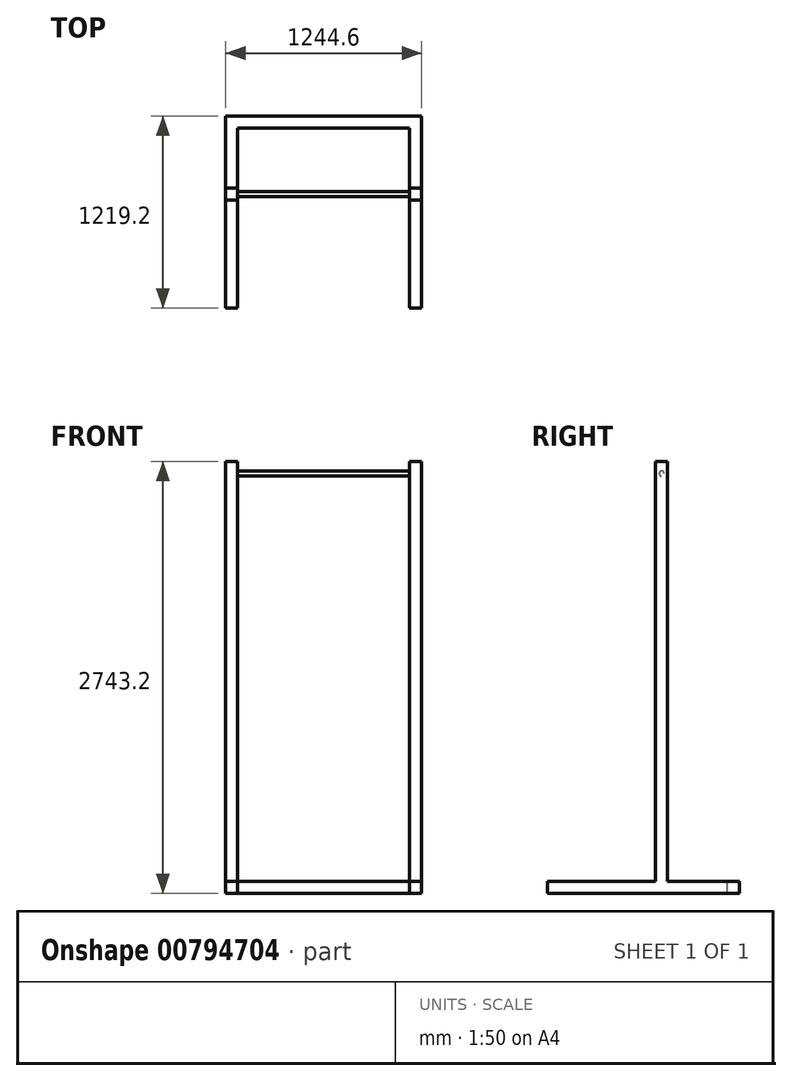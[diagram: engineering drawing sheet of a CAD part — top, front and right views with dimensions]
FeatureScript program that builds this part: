
annotation { "Feature Type Name" : "Feature", "Feature Type Description" : "" }
export const myFeature = defineFeature(function(context is Context, id is Id, definition is map)
    precondition{}
    {
        {
            var Q0;
            Q0=qCreatedBy(makeId("Top.planeOp"),FACE);
            var sketch = newSketch(context, id + "F0", { "sketchPlane" : qUnion([Q0])});
            skLineSegment(sketch, "E0.rect.bottom", {"start": v(-622.3, -609.6) * mm, "end": v(622.3, -609.6) * mm});
            skLineSegment(sketch, "E0.rect.top", {"start": v(-622.3, 609.6) * mm, "end": v(622.3, 609.6) * mm});
            skLineSegment(sketch, "E0.rect.left", {"start": v(-622.3, -609.6) * mm, "end": v(-622.3, 609.6) * mm});
            skLineSegment(sketch, "E0.rect.right", {"start": v(622.3, -609.6) * mm, "end": v(622.3, 609.6) * mm});
            skPoint(sketch, "E0.rect.middle", {"position": v(0, 0) * mm});
            skSolve(sketch);
        }
        {
            var Q0;
            Q0=makeQuery(id+"F0.imprint","IMPRINT",FACE,{"disambiguationData":[TD([[makeQuery(id+"F0.imprint","IMPRINT",EDGE,{"derivedFrom":sQuery(id+"F0.wireOp",EDGE,"E0.rect.bottom")}),1.0]])]});
            extrude(context, id + "F1", {"entities" : qUnion([Q0]), "depth" : 2743.2 * mm});
        }
        {
            var Q0;
            Q0=makeQuery(id+"F1.opExtrude","CAP_FACE",FACE,{"disambiguationData":[OSD([sQuery(id+"F0.wireOp",EDGE,"E0.rect.bottom"),sQuery(id+"F0.wireOp",EDGE,"E0.rect.top"),sQuery(id+"F0.wireOp",EDGE,"E0.rect.left"),sQuery(id+"F0.wireOp",EDGE,"E0.rect.right")])],"isStart":false});
            var sketch = newSketch(context, id + "F2", { "sketchPlane" : qUnion([Q0])});
            skLineSegment(sketch, "E1.bottom", {"start": v(-546.1, -609.6) * mm, "end": v(546.1, -609.6) * mm});
            skLineSegment(sketch, "E1.top", {"start": v(-546.1, 533.4) * mm, "end": v(546.1, 533.4) * mm});
            skLineSegment(sketch, "E1.left", {"start": v(-546.1, -609.6) * mm, "end": v(-546.1, 533.4) * mm});
            skLineSegment(sketch, "E1.right", {"start": v(546.1, -609.6) * mm, "end": v(546.1, 533.4) * mm});
            skPoint(sketch, "E2", {"position": v(0, -609.6) * mm});
            skSolve(sketch);
        }
        {
            var Q0;
            Q0=makeQuery(id+"F2.imprint","IMPRINT",FACE,{"disambiguationData":[TD([[makeQuery(id+"F2.imprint","IMPRINT",EDGE,{"derivedFrom":sQuery(id+"F2.wireOp",EDGE,"E1.bottom")}),1.0]])]});
            extrude(context, id + "F3", {"entities" : qUnion([Q0]), "operationType" : NewBodyOperationType.REMOVE, "endBound" : BoundingType.THROUGH_ALL, "oppositeDirection" : true, "depth" : 25.4 * mm});
        }
        {
            var Q0;
            Q0=makeQuery(id+"F1.opExtrude","CAP_FACE",FACE,{"disambiguationData":[OSD([sQuery(id+"F0.wireOp",EDGE,"E0.rect.bottom"),sQuery(id+"F0.wireOp",EDGE,"E0.rect.top"),sQuery(id+"F0.wireOp",EDGE,"E0.rect.left"),sQuery(id+"F0.wireOp",EDGE,"E0.rect.right")])],"isStart":false});
            var sketch = newSketch(context, id + "F4", { "sketchPlane" : qUnion([Q0])});
            skLineSegment(sketch, "E3.bottom", {"start": v(-622.3, 609.6) * mm, "end": v(622.3, 609.6) * mm});
            skLineSegment(sketch, "E3.top", {"start": v(-622.3, 152.4) * mm, "end": v(622.3, 152.4) * mm});
            skLineSegment(sketch, "E3.left", {"start": v(-622.3, 609.6) * mm, "end": v(-622.3, 152.4) * mm});
            skLineSegment(sketch, "E3.right", {"start": v(622.3, 609.6) * mm, "end": v(622.3, 152.4) * mm});
            skLineSegment(sketch, "E4.bottom", {"start": v(-622.3, -609.6) * mm, "end": v(622.3, -609.6) * mm});
            skLineSegment(sketch, "E4.top", {"start": v(-622.3, 76.2) * mm, "end": v(622.3, 76.2) * mm});
            skLineSegment(sketch, "E4.left", {"start": v(-622.3, -609.6) * mm, "end": v(-622.3, 76.2) * mm});
            skLineSegment(sketch, "E4.right", {"start": v(622.3, -609.6) * mm, "end": v(622.3, 76.2) * mm});
            skSolve(sketch);
        }
        {
            var Q0;
            Q0=makeQuery(id+"F4.imprint","IMPRINT",FACE,{"disambiguationData":[TD([[makeQuery(id+"F4.imprint","IMPRINT",EDGE,{"derivedFrom":sQuery(id+"F4.wireOp",EDGE,"E3.bottom")}),-1.0]])]});
            var Q1;
            {var subQ5=sQuery(id+"F4.wireOp",EDGE,"E4.left");Q1=makeQuery(id+"F4.imprint","IMPRINT",FACE,{"disambiguationData":[TD([[makeQuery(id+"F4.imprint","IMPRINT",EDGE,{"derivedFrom":subQ5}),-1.0]])]});}
            var Q2;
            {var subQ5=sQuery(id+"F4.wireOp",EDGE,"E4.right");Q2=makeQuery(id+"F4.imprint","IMPRINT",FACE,{"disambiguationData":[TD([[makeQuery(id+"F4.imprint","IMPRINT",EDGE,{"derivedFrom":subQ5}),1.0]])]});}
            extrude(context, id + "F5", {"entities" : qUnion([Q0, Q1, Q2]), "operationType" : NewBodyOperationType.REMOVE, "oppositeDirection" : true, "depth" : 2667 * mm});
        }
        {
            var Q0;
            Q0=makeQuery(id+"F3.boolean.opBoolean","COPY",FACE,{"derivedFrom":makeQuery(id+"F3.opExtrude","SWEPT_FACE",FACE,{"disambiguationData":[OSD([sQuery(id+"F2.wireOp",EDGE,"E1.left")])]})});
            var sketch = newSketch(context, id + "F6", { "sketchPlane" : qUnion([Q0])});
            skCircle(sketch, "E5", {"center": v(114.3, 2667) * mm, "radius": 15.88 * mm});
            skLineSegment(sketch, "E6", {"start": v(76.2, 2667) * mm, "end": v(152.4, 2667) * mm, "construction": true});
            skSolve(sketch);
        }
        {
            var Q0;
            Q0=makeQuery(id+"F6.imprint","IMPRINT",FACE,{"disambiguationData":[TD([[makeQuery(id+"F6.imprint","IMPRINT",EDGE,{"derivedFrom":sQuery(id+"F6.wireOp",EDGE,"E5")}),1.0]])]});
            var Q1;
            Q1=makeQuery(id+"F3.boolean.opBoolean","COPY",FACE,{"derivedFrom":makeQuery(id+"F3.opExtrude","SWEPT_FACE",FACE,{"disambiguationData":[OSD([sQuery(id+"F2.wireOp",EDGE,"E1.right")])]})});
            extrude(context, id + "F7", {"entities" : qUnion([Q0]), "operationType" : NewBodyOperationType.ADD, "endBound" : BoundingType.UP_TO_SURFACE, "endBoundEntityFace" : qUnion([Q1]), "depth" : 25.4 * mm});
        }
    });
